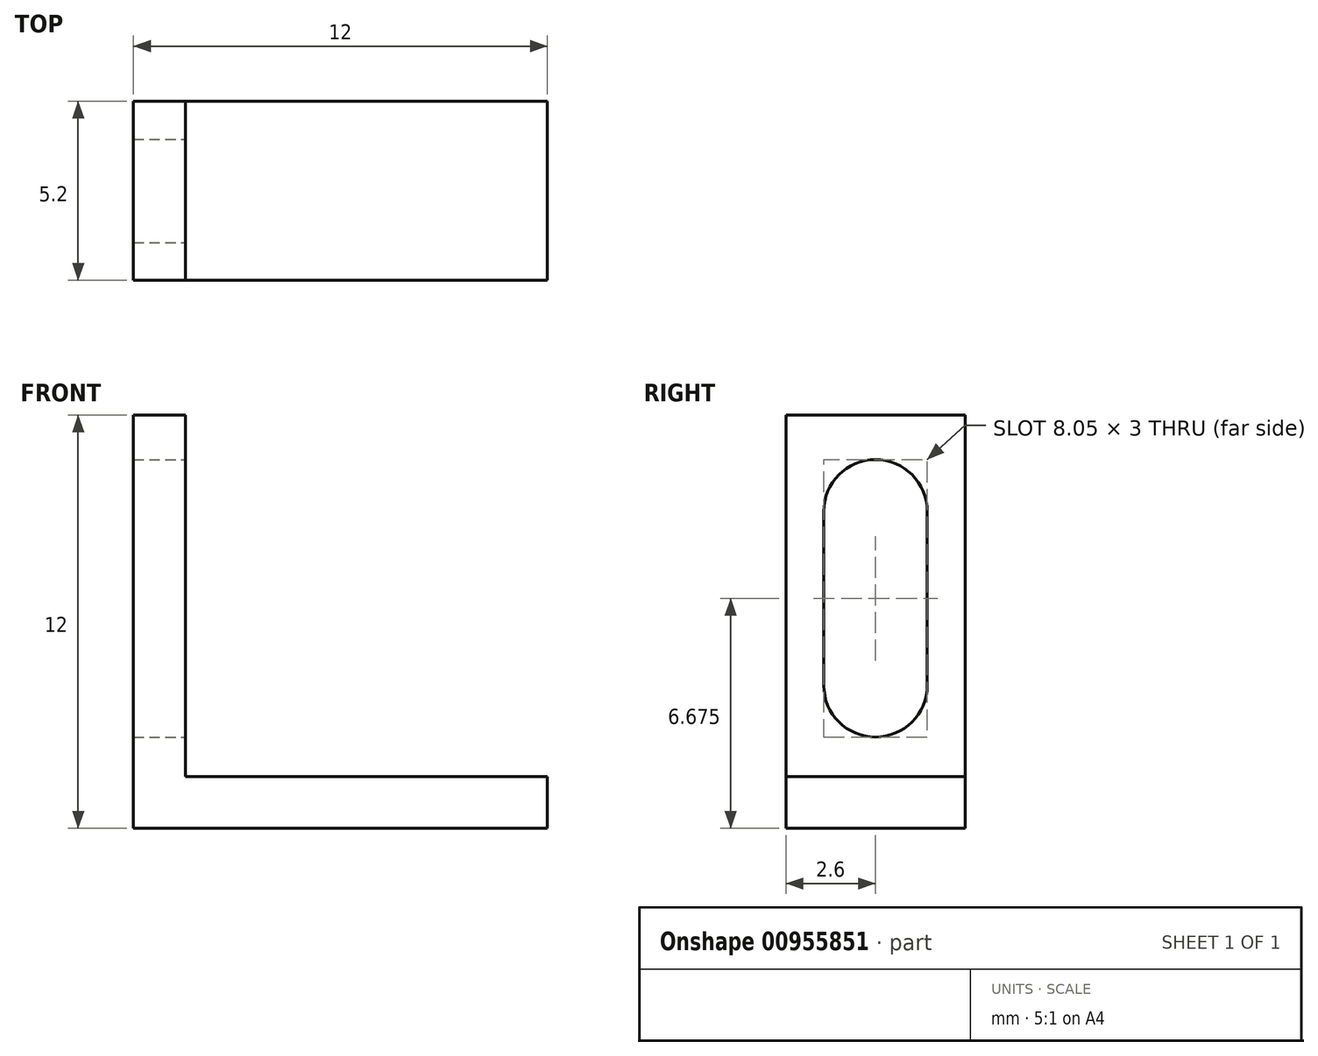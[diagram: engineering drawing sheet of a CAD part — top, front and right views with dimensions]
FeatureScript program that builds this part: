
annotation { "Feature Type Name" : "Feature", "Feature Type Description" : "" }
export const myFeature = defineFeature(function(context is Context, id is Id, definition is map)
    precondition{}
    {
        {
            var Q0;
            Q0=qCreatedBy(makeId("Front.planeOp"),FACE);
            var sketch = newSketch(context, id + "F0", { "sketchPlane" : qUnion([Q0])});
            skLineSegment(sketch, "E0", {"start": v(0, 0) * mm, "end": v(0, -12) * mm});
            skLineSegment(sketch, "E1", {"start": v(0, -12) * mm, "end": v(12, -12) * mm});
            skLineSegment(sketch, "E2", {"start": v(12, -12) * mm, "end": v(12, -10.5) * mm});
            skLineSegment(sketch, "E3", {"start": v(12, -10.5) * mm, "end": v(1.5, -10.5) * mm});
            skLineSegment(sketch, "E4", {"start": v(1.5, -10.5) * mm, "end": v(1.5, 0) * mm});
            skLineSegment(sketch, "E5", {"start": v(1.5, 0) * mm, "end": v(0, 0) * mm});
            skSolve(sketch);
        }
        {
            var Q0;
            Q0=makeQuery(id+"F0.imprint","IMPRINT",FACE,{"disambiguationData":[TD([[makeQuery(id+"F0.imprint","IMPRINT",EDGE,{"derivedFrom":sQuery(id+"F0.wireOp",EDGE,"E0")}),1.0]])]});
            extrude(context, id + "F1", {"entities" : qUnion([Q0]), "depth" : 5.2 * mm, "offsetDistance" : 25 * mm});
        }
        {
            var Q0;
            Q0=makeQuery(id+"F1.opExtrude","SWEPT_FACE",FACE,{"disambiguationData":[OSD([sQuery(id+"F0.wireOp",EDGE,"E4")])]});
            var sketch = newSketch(context, id + "F2", { "sketchPlane" : qUnion([Q0])});
            skPoint(sketch, "E6", {"position": v(-2.6, -1.3) * mm});
            skLineSegment(sketch, "E7.left", {"start": v(-1.1, -7.85) * mm, "end": v(-1.1, -2.8) * mm});
            skLineSegment(sketch, "E7.right", {"start": v(-4.1, -7.85) * mm, "end": v(-4.1, -2.8) * mm});
            skArc(sketch, "E8", {"start": v(-1.1, -2.8) * mm, "mid": v(-2.6, -1.3) * mm, "end": v(-4.1, -2.8) * mm});
            skPoint(sketch, "E9", {"position": v(-2.6, -9.35) * mm});
            skPoint(sketch, "E9.positionSnap0", {"position": v(-2.6, -7.85) * mm});
            skArc(sketch, "E10", {"start": v(-4.1, -7.85) * mm, "mid": v(-2.6, -9.35) * mm, "end": v(-1.1, -7.85) * mm});
            skSolve(sketch);
        }
        {
            var Q0;
            Q0=makeQuery(id+"F2.imprint","IMPRINT",FACE,{"disambiguationData":[TD([[makeQuery(id+"F2.imprint","IMPRINT",EDGE,{"derivedFrom":sQuery(id+"F2.wireOp",EDGE,"E7.left")}),1.0]])]});
            extrude(context, id + "F3", {"entities" : qUnion([Q0]), "operationType" : NewBodyOperationType.REMOVE, "oppositeDirection" : true, "depth" : 25 * mm, "offsetDistance" : 25 * mm});
        }
    });
